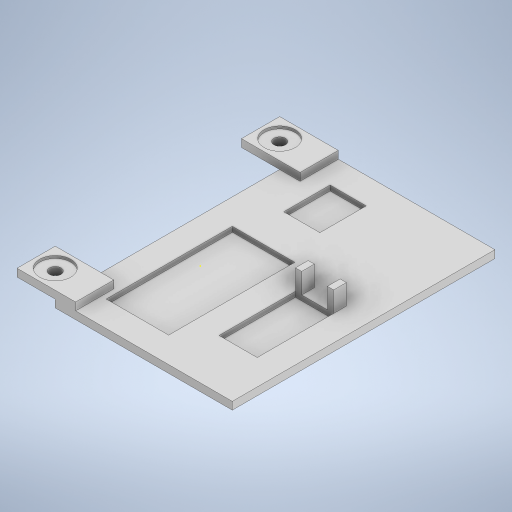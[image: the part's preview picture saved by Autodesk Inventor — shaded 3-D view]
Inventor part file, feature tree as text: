
AUTODESK INVENTOR PART (.ipt)
format: ipt  version: 2024 (Build 280153000, 153)  size: 358,400 bytes
history: native  units: in
note: dims shown in document units (in); Inventor stores cm internally (conversion verified against a paired STEP export)
features: sketch x8, extrude x7
ambient origin geometry x8: Origin, YZ Plane, XZ Plane, XY Plane, X Axis, Y Axis, Z Axis, Center Point
bodies: Solid1 (feature_tree)
feature tree (15):
  extrude  "Extrusion1"  Depth=1.9488in
  extrude  "Extrusion2"  Depth=1.1811in
  sketch  "Sketch3"  dims[d4=0.3937in d7=0.5591in]
  extrude  "Extrusion3"  Depth=0.5591in
  extrude  "Extrusion5"  Depth=0.5906in
  extrude  "Extrusion6"  Depth=4.0591in
  extrude  "Extrusion7"  Depth=0.3937in
  extrude  "Extrusion8"  Depth=0.0787in TaperAngle=0.0deg
  sketch  "Sketch1"  dims[d0=0.9646in d1=1.9488in]
  sketch  "Sketch2"  dims[d2=0.5906in d3=1.1811in]
  sketch  "Sketch4"  dims[d8=0.7165in d9=0.5906in]
  sketch  "Sketch7"  dims[d17=0.3937in d19=4.0591in]
  sketch  "Sketch8"  dims[d21=0.3937in d22=0.3937in]
  sketch  "Sketch9"  dims[d23=0.1181in d24=0.0in]
  sketch  "Sketch10"  dims[d25=0.9646in d26=1.9488in d27=0.5906in d28=1.1811in d29=0.3937in d30=0.5591in d31=0.7165in d32=0.5906in d33=0.5906in d34=0.5906in d35=0.5906in d36=0.5906in d37=0.3937in d38=0.4646in d39=4.0591in d40=0.3937in d41=0.3937in d42=0.0787in d43=0.0in d44=0.3976in d45=0.1969in d46=0.1969in d47=0.315in d48=0.0in d52=0.5906in d53=0.5906in d54=0.5906in d55=0.5906in d56=0.315in d57=0.1181in d58=0.0in d59=0.1772in d60=0.1772in d61=0.1181in d62=0.0in d63=0.4803in d64=0.4803in d65=0.0394in d66=0.0in d67=0.4803in d68=0.4803in d69=0.0394in d70=0.0in]
